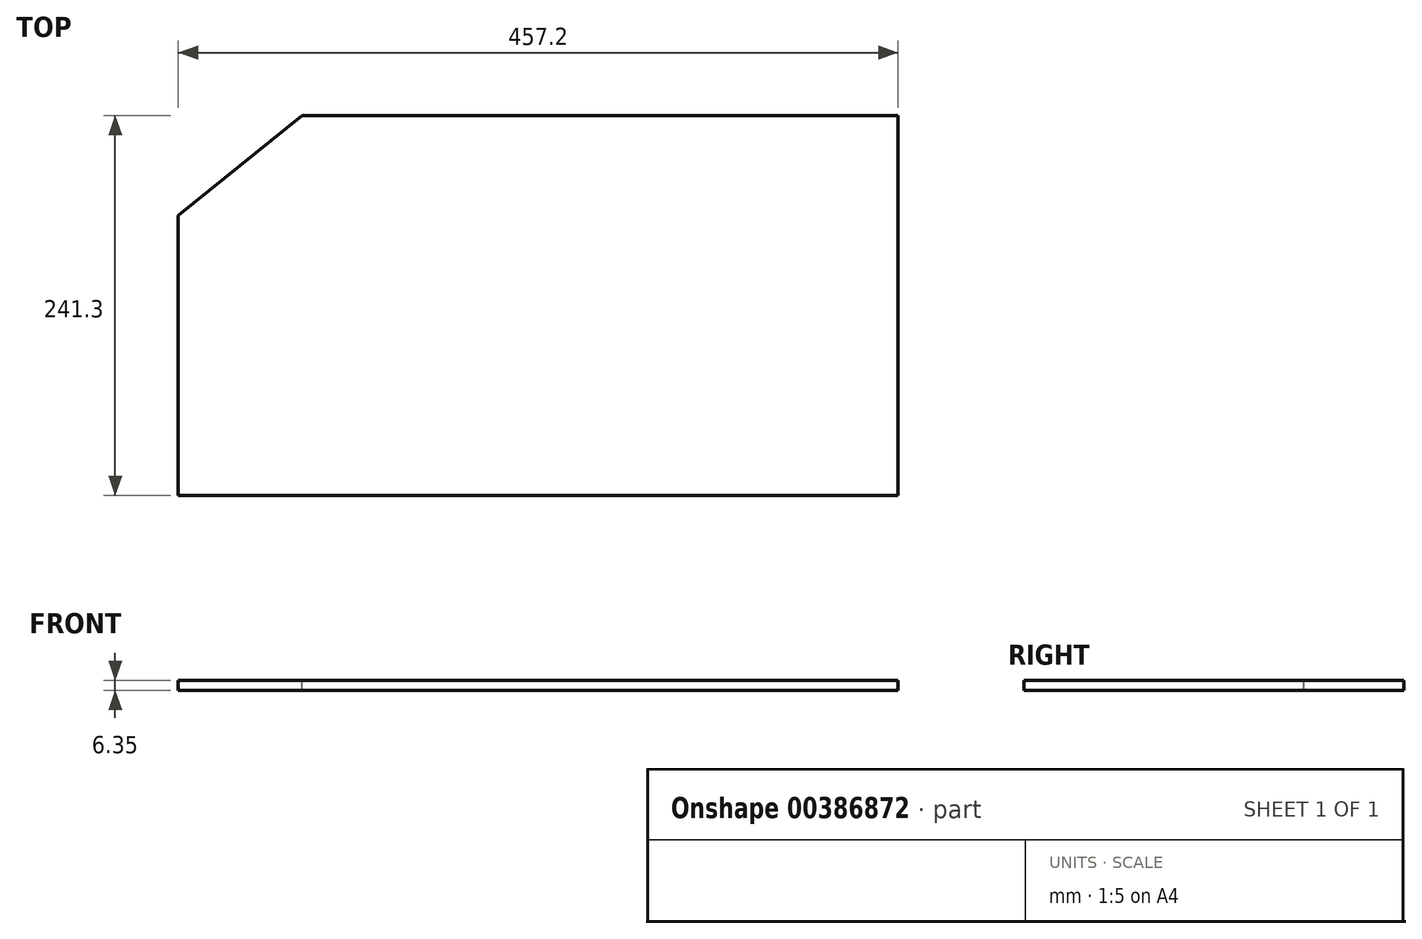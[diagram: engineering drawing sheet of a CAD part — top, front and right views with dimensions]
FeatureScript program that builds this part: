
annotation { "Feature Type Name" : "Feature", "Feature Type Description" : "" }
export const myFeature = defineFeature(function(context is Context, id is Id, definition is map)
    precondition{}
    {
        {
            var Q0;
            Q0=qCreatedBy(makeId("Top.planeOp"),FACE);
            var sketch = newSketch(context, id + "F0", { "sketchPlane" : qUnion([Q0])});
            skLineSegment(sketch, "E0.bottom", {"start": v(228.6, 120.65) * mm, "end": v(-228.6, 120.65) * mm});
            skLineSegment(sketch, "E0.top", {"start": v(228.6, -120.65) * mm, "end": v(-228.6, -120.65) * mm});
            skLineSegment(sketch, "E0.left", {"start": v(228.6, 120.65) * mm, "end": v(228.6, -120.65) * mm});
            skLineSegment(sketch, "E0.right", {"start": v(-228.6, 120.65) * mm, "end": v(-228.6, -120.65) * mm});
            skPoint(sketch, "E0.middle", {"position": v(0, 0) * mm});
            skSolve(sketch);
        }
        {
            var Q0;
            Q0=makeQuery(id+"F0.imprint","IMPRINT",FACE,{"disambiguationData":[TD([[makeQuery(id+"F0.imprint","IMPRINT",EDGE,{"derivedFrom":sQuery(id+"F0.wireOp",EDGE,"E0.bottom")}),1.0]])]});
            extrude(context, id + "F1", {"entities" : qUnion([Q0]), "depth" : 6.35 * mm, "offsetDistance" : 25.4 * mm});
        }
        {
            var Q0;
            Q0=makeQuery(id+"F1.opExtrude","CAP_FACE",FACE,{"disambiguationData":[OSD([sQuery(id+"F0.wireOp",EDGE,"E0.bottom"),sQuery(id+"F0.wireOp",EDGE,"E0.top"),sQuery(id+"F0.wireOp",EDGE,"E0.left"),sQuery(id+"F0.wireOp",EDGE,"E0.right")])],"isStart":false});
            var sketch = newSketch(context, id + "F2", { "sketchPlane" : qUnion([Q0])});
            skLineSegment(sketch, "E1", {"start": v(-228.6, 57.15) * mm, "end": v(-149.86, 120.65) * mm});
            skLineSegment(sketch, "E2", {"start": v(-149.86, 120.65) * mm, "end": v(-228.6, 120.65) * mm});
            skLineSegment(sketch, "E3", {"start": v(-228.6, 120.65) * mm, "end": v(-228.6, 57.15) * mm});
            skSolve(sketch);
        }
        {
            var Q0;
            Q0 = qSketchRegion(id + "F2", true);
            extrude(context, id + "F3", {"entities" : qUnion([Q0]), "operationType" : NewBodyOperationType.REMOVE, "oppositeDirection" : true, "depth" : 6.35 * mm, "offsetDistance" : 25.4 * mm});
        }
    });
